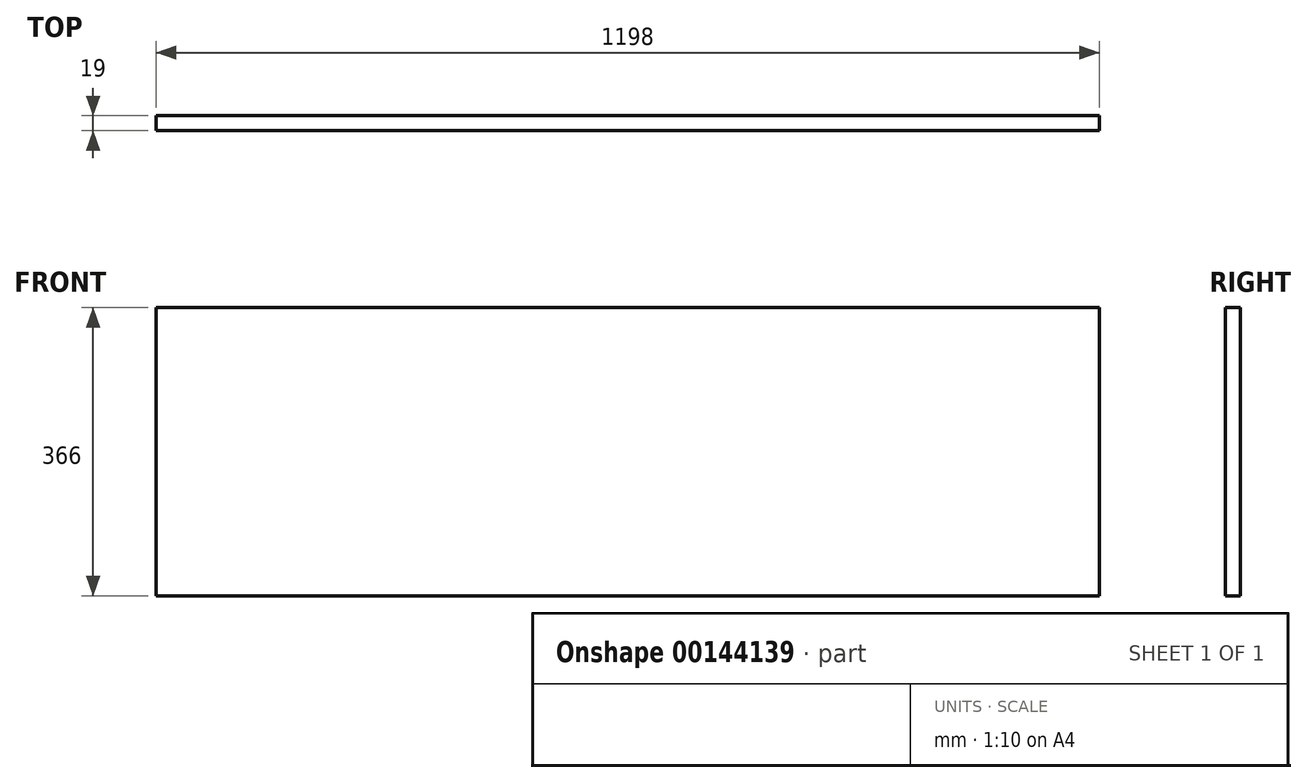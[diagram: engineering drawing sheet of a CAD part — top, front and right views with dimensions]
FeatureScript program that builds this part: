
annotation { "Feature Type Name" : "Feature", "Feature Type Description" : "" }
export const myFeature = defineFeature(function(context is Context, id is Id, definition is map)
    precondition{}
    {
        {
            var Q0;
            Q0=qCreatedBy(makeId("Front.planeOp"),FACE);
            var sketch = newSketch(context, id + "F0", { "sketchPlane" : qUnion([Q0])});
            skLineSegment(sketch, "E0.bottom", {"start": v(0, 0) * mm, "end": v(1198, 0) * mm});
            skLineSegment(sketch, "E0.top", {"start": v(0, 366) * mm, "end": v(1198, 366) * mm});
            skLineSegment(sketch, "E0.left", {"start": v(0, 0) * mm, "end": v(0, 366) * mm});
            skLineSegment(sketch, "E0.right", {"start": v(1198, 0) * mm, "end": v(1198, 366) * mm});
            skSolve(sketch);
        }
        {
            var Q0;
            Q0=makeQuery(id+"F0.imprint","IMPRINT",FACE,{"disambiguationData":[TD([[makeQuery(id+"F0.imprint","IMPRINT",EDGE,{"derivedFrom":sQuery(id+"F0.wireOp",EDGE,"E0.bottom")}),1.0]])]});
            extrude(context, id + "F1", {"entities" : qUnion([Q0]), "depth" : 19 * mm});
        }
    });
